# Revit family: RV 5000 01  Boxter carril
name_source: partatom
category: Luminarias
revit_build: Autodesk Revit 2015 (Build: 20140606_1530(x64)
units: mm (PartAtom-declared; Revit-internal decimal feet)

## types (9) — shared parameters
Cambio de temperatura de color de luz atenuada = <Ninguno>
Diámetro de círculo de emisión = 78 mm  [stored 0.255906 ft]
Fabricante = Secom Iluminación
Filtro de color = 16777215
Forma visible en renderización = No
Lámpara = LED Osram Oslon SSL
Modelo = Boxter Carril
Ángulo de inclinación = 90.00°

## per-type parameters (varying)
| type | Archivo de red fotométrica | Comentarios de vataje | Descripción |
| Boxter Carril 13W Óptica estandar 54º | 5000 01 13 84 - BOXTER LED 54º ABIERTO.IES | 13 W | 5000 01 13 84    óptica 54º |
| Boxter Carril 13 W Óptica 16º | 5000 01 13 84 - BOXTER LED 16º ABIERTO.IES | 13 W | 5000 01 13 84    óptica 16º |
| Boxter Carill 13 W Óptica 28º | 5000 01 13 84 - BOXTER LED 28º ABIERTO.IES | 13 W | 5000 01 13 84    óptica 28º |
| Boxter Carril 26 W Óptica estandar 54º | 5000 01 26 84 - BOXTER LED 54º ABIERTO.IES | 26 W | 5000 01 26 84    óptica 54º |
| Boxter Carril 26 W Óptica 28º | 5000 01 26 84 - BOXTER LED 28º ABIERTO.IES | 26 W | 5000 01 26 84    óptica 28º |
| Boxter Carril 26 W Óptica 16º | 5000 01 26 84 - BOXTER LED 16º ABIERTO.IES | 26 W | 5000 01 26 84    óptica 16º |
| Boxter Carril 31 W Óptica estandar 54º | 5000 01 31 84 - BOXTER LED 54º ABIERTO.IES | 31 W | 5000 01 31 84    óptica 54º |
| Boxter Carril 31 W Óptica 16º | 5000 01 31 84 - BOXTER LED 16º ABIERTO.IES | 31 W | 5000 01 31 84    óptica 16º |
| Boxter Carril 31 W Óptica 28º | 5000 01 31 84 - BOXTER LED 28º ABIERTO.IES | 31 W | 5000 01 31 84    óptica 28º |

note: [stored X ft] marks values corroborated as IEEE doubles in the binary element streams (Revit-internal decimal feet)
